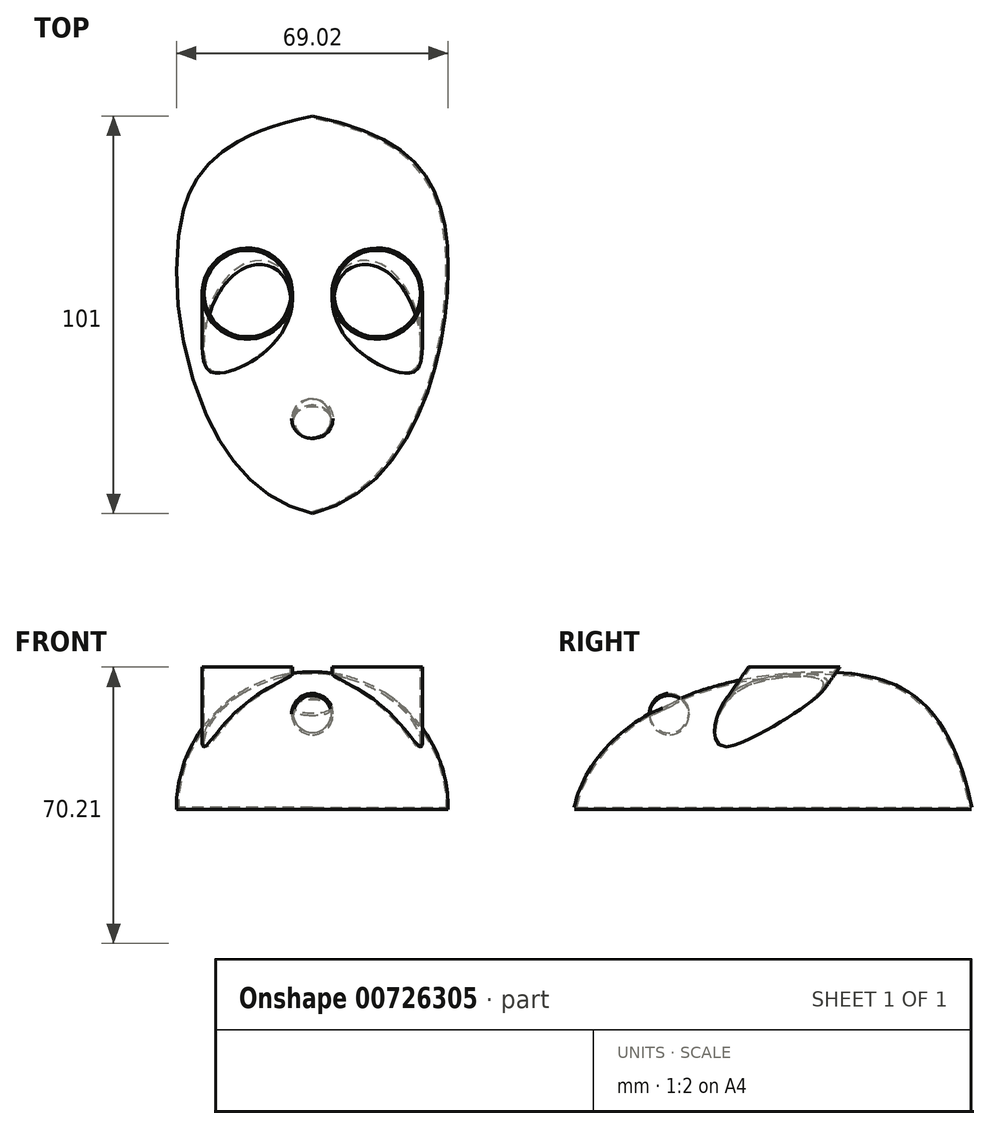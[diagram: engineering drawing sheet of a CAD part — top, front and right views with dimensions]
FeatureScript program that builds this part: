
annotation { "Feature Type Name" : "Feature", "Feature Type Description" : "" }
export const myFeature = defineFeature(function(context is Context, id is Id, definition is map)
    precondition{}
    {
        {
            var Q0;
            Q0=qCreatedBy(makeId("Right.planeOp"),FACE);
            var sketch = newSketch(context, id + "F0", { "sketchPlane" : qUnion([Q0])});
            skFitSpline(sketch, "E0", {"points": [v(-49, -8) * mm, v(17, 25.88) * mm, v(51, -8) * mm], "startDerivative": vector(33.33, 142.3) * mm, "endDerivative": vector(35.32, -168.77) * mm});
            skLineSegment(sketch, "E1", {"start": v(-49, -8) * mm, "end": v(51, -8) * mm});
            skSolve(sketch);
        }
        {
            var Q0;
            Q0=makeQuery(id+"F0.imprint","IMPRINT",FACE,{"disambiguationData":[TD([[makeQuery(id+"F0.imprint","IMPRINT",EDGE,{"derivedFrom":sQuery(id+"F0.wireOp",EDGE,"E0")}),-1.0]])]});
            var Q1;
            Q1=sQuery(id+"F0.wireOp",EDGE,"E1");
            revolve(context, id + "F1", {"surfaceOperationType" : NewSurfaceOperationType.NEW, "entities" : qUnion([Q0]), "axis" : qUnion([Q1]), "revolveType" : RevolveType.SYMMETRIC, "angle" : 180 * degree});
        }
        {
            var Q0;
            Q0=qCreatedBy(makeId("Top.planeOp"),FACE);
            var sketch = newSketch(context, id + "F2", { "sketchPlane" : qUnion([Q0])});
            skCircle(sketch, "E2", {"center": v(-16.5, -13) * mm, "radius": 11 * mm});
            skCircle(sketch, "E3.MirrorC", {"center": v(16.5, -13) * mm, "radius": 11 * mm});
            skSolve(sketch);
        }
        {
            var Q0;
            Q0=qCreatedBy(makeId("Right.planeOp"),FACE);
            var sketch = newSketch(context, id + "F3", { "sketchPlane" : qUnion([Q0])});
            skLineSegment(sketch, "E4", {"start": v(-10, -8) * mm, "end": v(15, 27.7) * mm});
            skSolve(sketch);
        }
        {
            var Q0;
            Q0=qSketchRegion(id+"F2",true);
            var Q1;
            Q1=qConstructionFilter(qBodyType(qCreatedBy(id+"F3",EDGE),BodyType.WIRE),ConstructionObject.NO);
            sweep(context, id + "F4", {"operationType" : NewBodyOperationType.ADD, "profiles" : qUnion([Q0]), "path" : qUnion([Q1])});
        }
        {
            var Q0;
            Q0=makeQuery(id+"F4.opSweep","CAP_FACE",FACE,{"disambiguationData":[OSD([sQuery(id+"F2.wireOp",EDGE,"1IkE4SMT-ChKx-BDRj-Jc3O-eQ57HxbeEk25"),sQuery(id+"F3.wireOp",VERTEX,"E4.end")])],"isStart":false});
            shell(context, id + "F5", {"entities" : qUnion([Q0]), "thickness" : 0.5 * mm, "oppositeDirection" : true});
        }
        {
            var Q0;
            Q0=qCreatedBy(makeId("Right.planeOp"),FACE);
            var sketch = newSketch(context, id + "F6", { "sketchPlane" : qUnion([Q0])});
            skArc(sketch, "E5", {"start": v(-20.38, 16) * mm, "mid": v(-25.63, 21) * mm, "end": v(-30.35, 15.5) * mm});
            skLineSegment(sketch, "E6", {"start": v(-30.35, 15.5) * mm, "end": v(-20.38, 16) * mm});
            skSolve(sketch);
        }
        {
            var Q0;
            Q0=makeQuery(id+"F6.imprint","IMPRINT",FACE,{"disambiguationData":[TD([[makeQuery(id+"F6.imprint","IMPRINT",EDGE,{"derivedFrom":sQuery(id+"F6.wireOp",EDGE,"E5")}),1.0]])]});
            var Q1;
            Q1=sQuery(id+"F6.wireOp",EDGE,"E6");
            revolve(context, id + "F7", {"surfaceOperationType" : NewSurfaceOperationType.NEW, "entities" : qUnion([Q0]), "axis" : qUnion([Q1]), "revolveType" : RevolveType.FULL});
        }
        {
            var Q0;
            Q0=makeQuery(id+"F7.opRevolve","SWEPT_BODY",BODY,{"disambiguationData":[OSD([sQuery(id+"F6.wireOp",EDGE,"E5"),sQuery(id+"F6.wireOp",EDGE,"E6")])]});
            var Q1;
            Q1=makeQuery(id+"F1.opRevolve","SWEPT_BODY",BODY,{"disambiguationData":[OSD([sQuery(id+"F0.wireOp",EDGE,"E0"),sQuery(id+"F0.wireOp",EDGE,"E1")])]});
            booleanBodies(context, id + "F8", {"operationType" : BooleanOperationType.SUBTRACTION, "tools" : qUnion([Q0]), "targets" : qUnion([Q1]), "keepTools" : true});
        }
    });
